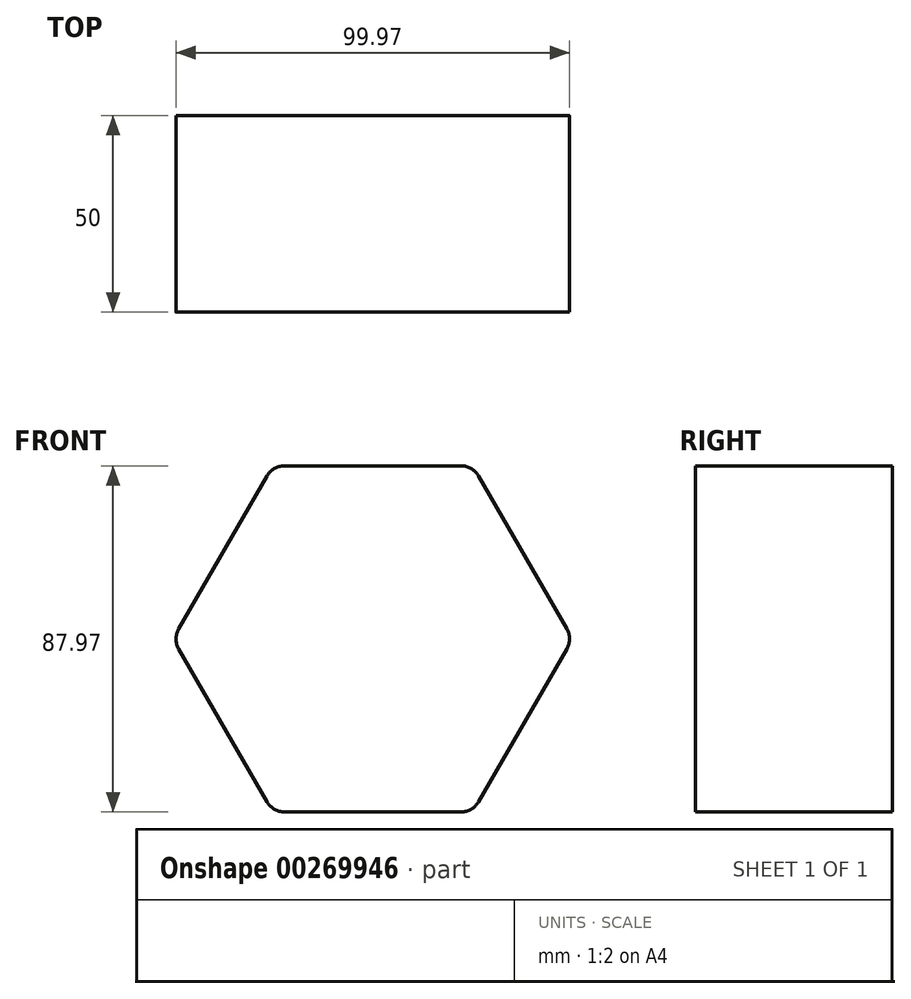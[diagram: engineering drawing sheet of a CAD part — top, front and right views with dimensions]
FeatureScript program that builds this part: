
annotation { "Feature Type Name" : "Feature", "Feature Type Description" : "" }
export const myFeature = defineFeature(function(context is Context, id is Id, definition is map)
    precondition{}
    {
        {
            var Q0;
            Q0=qCreatedBy(makeId("Front.planeOp"),FACE);
            var sketch = newSketch(context, id + "F0", { "sketchPlane" : qUnion([Q0])});
            skCircle(sketch, "E0.cCircle", {"center": v(-123.04, 43.76) * mm, "radius": 43.97 * mm, "construction": true});
            skLineSegment(sketch, "E0.0", {"start": v(-72.27, 43.8) * mm, "end": v(-97.61, -0.18) * mm});
            skLineSegment(sketch, "E0.1", {"start": v(-97.61, -0.18) * mm, "end": v(-148.38, -0.23) * mm});
            skLineSegment(sketch, "E0.2", {"start": v(-148.38, -0.23) * mm, "end": v(-173.8, 43.72) * mm});
            skLineSegment(sketch, "E0.3", {"start": v(-173.8, 43.72) * mm, "end": v(-148.46, 87.7) * mm});
            skLineSegment(sketch, "E0.4", {"start": v(-148.46, 87.7) * mm, "end": v(-97.69, 87.75) * mm});
            skLineSegment(sketch, "E0.5", {"start": v(-97.69, 87.75) * mm, "end": v(-72.27, 43.8) * mm});
            skPoint(sketch, "E0.0.midPoint", {"position": v(-84.94, 21.81) * mm});
            skSolve(sketch);
        }
        {
            var Q0;
            Q0 = qSketchRegion(id + "F0", true);
            extrude(context, id + "F1", {"entities" : qUnion([Q0]), "depth" : 50 * mm});
        }
        {
            var Q0;
            Q0=makeQuery(id+"F1.opExtrude","SWEPT_EDGE",EDGE,{"disambiguationData":[OSD([sQuery(id+"F0.wireOp",EDGE,"E0.4"),sQuery(id+"F0.wireOp",EDGE,"E0.5")])]});
            var Q1;
            Q1=makeQuery(id+"F1.opExtrude","SWEPT_EDGE",EDGE,{"disambiguationData":[OSD([sQuery(id+"F0.wireOp",EDGE,"E0.0"),sQuery(id+"F0.wireOp",EDGE,"E0.5")])]});
            var Q2;
            Q2=makeQuery(id+"F1.opExtrude","SWEPT_EDGE",EDGE,{"disambiguationData":[OSD([sQuery(id+"F0.wireOp",EDGE,"E0.0"),sQuery(id+"F0.wireOp",EDGE,"E0.1")])]});
            var Q3;
            Q3=makeQuery(id+"F1.opExtrude","SWEPT_EDGE",EDGE,{"disambiguationData":[OSD([sQuery(id+"F0.wireOp",EDGE,"E0.1"),sQuery(id+"F0.wireOp",EDGE,"E0.2")])]});
            var Q4;
            Q4=makeQuery(id+"F1.opExtrude","SWEPT_EDGE",EDGE,{"disambiguationData":[OSD([sQuery(id+"F0.wireOp",EDGE,"E0.2"),sQuery(id+"F0.wireOp",EDGE,"E0.3")])]});
            var Q5;
            Q5=makeQuery(id+"F1.opExtrude","SWEPT_EDGE",EDGE,{"disambiguationData":[OSD([sQuery(id+"F0.wireOp",EDGE,"E0.3"),sQuery(id+"F0.wireOp",EDGE,"E0.4")])]});
            fillet(context, id + "F2", {"entities" : qUnion([Q0, Q1, Q2, Q3, Q4, Q5]), "radius" : 5.08 * mm, "tangentPropagation" : true, "allowEdgeOverflow" : false});
        }
    });
